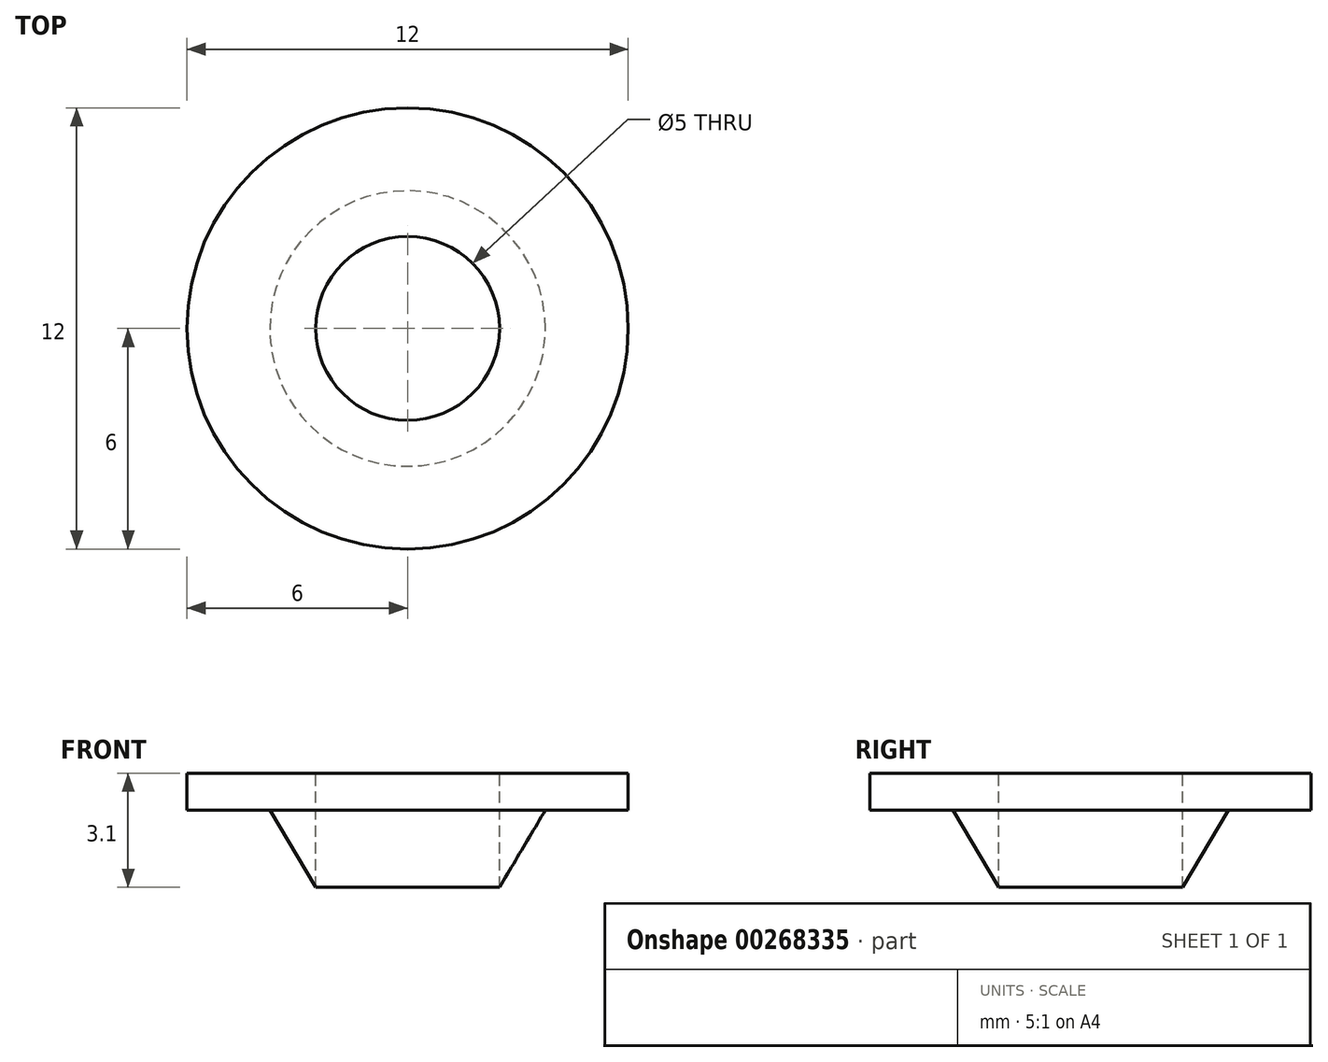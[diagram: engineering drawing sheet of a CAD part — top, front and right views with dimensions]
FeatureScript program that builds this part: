
annotation { "Feature Type Name" : "Feature", "Feature Type Description" : "" }
export const myFeature = defineFeature(function(context is Context, id is Id, definition is map)
    precondition{}
    {
        {
            var Q0;
            Q0=qCreatedBy(makeId("Front.planeOp"),FACE);
            var sketch = newSketch(context, id + "F0", { "sketchPlane" : qUnion([Q0])});
            skLineSegment(sketch, "E0", {"start": v(0, 6.77) * mm, "end": v(0, -2.47) * mm, "construction": true});
            skLineSegment(sketch, "E1", {"start": v(2.5, 0) * mm, "end": v(2.5, 3.1) * mm});
            skLineSegment(sketch, "E2", {"start": v(2.5, 3.1) * mm, "end": v(6, 3.1) * mm});
            skLineSegment(sketch, "E3", {"start": v(6, 3.1) * mm, "end": v(6, 2.1) * mm});
            skLineSegment(sketch, "E4", {"start": v(6, 2.1) * mm, "end": v(3.75, 2.1) * mm});
            skLineSegment(sketch, "E5", {"start": v(3.75, 2.1) * mm, "end": v(2.5, 0) * mm});
            skSolve(sketch);
        }
        {
            var Q0;
            Q0=qSketchRegion(id+"F0",true);
            var Q1;
            Q1=sQuery(id+"F0.wireOp",EDGE,"E0");
            revolve(context, id + "F1", {"entities" : qUnion([Q0]), "axis" : qUnion([Q1]), "revolveType" : RevolveType.FULL});
        }
    });
